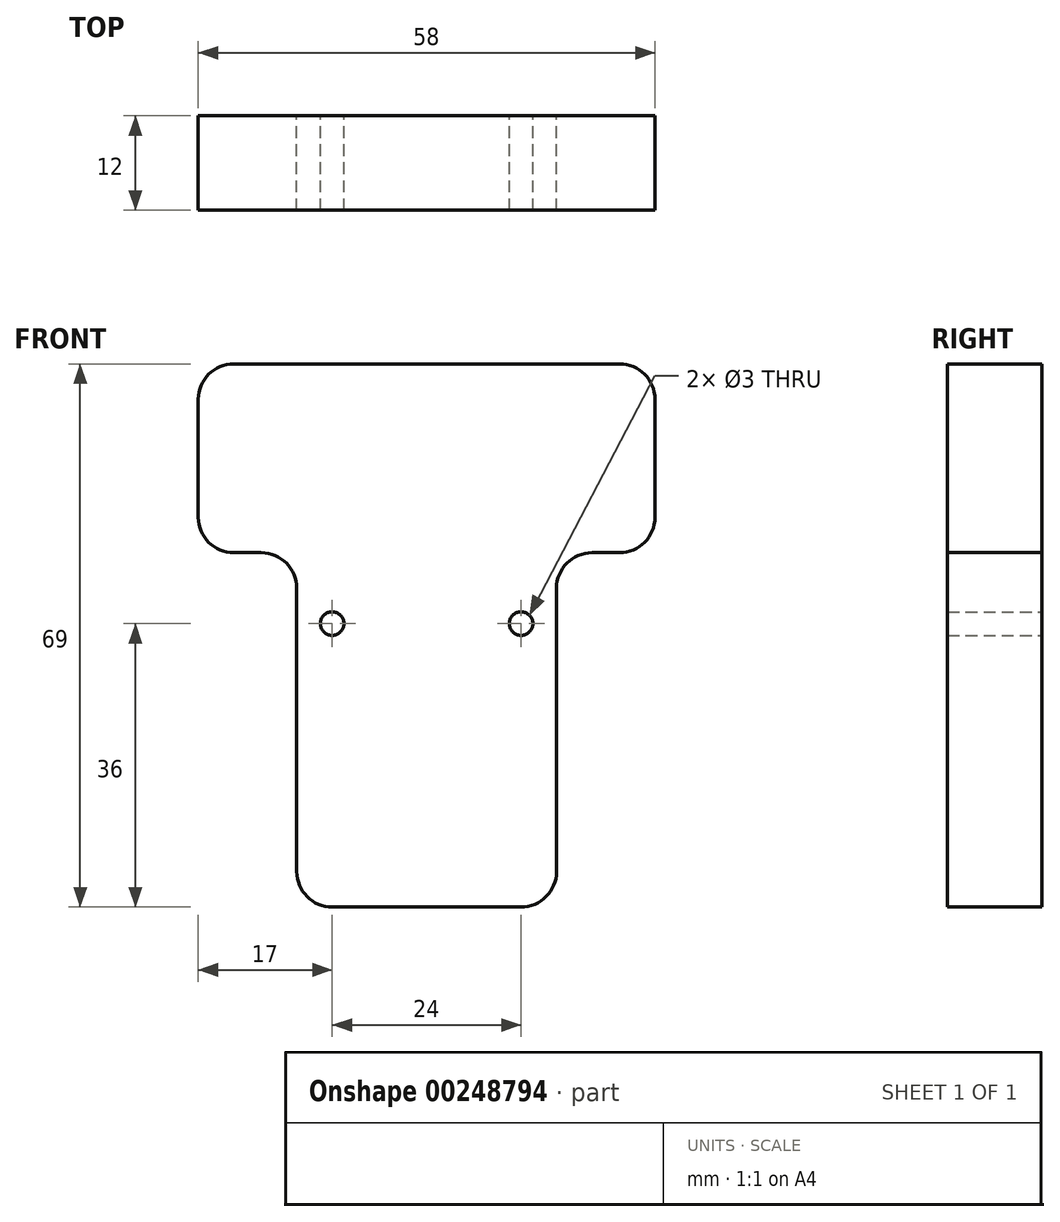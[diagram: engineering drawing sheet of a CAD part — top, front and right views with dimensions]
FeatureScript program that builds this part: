
annotation { "Feature Type Name" : "Feature", "Feature Type Description" : "" }
export const myFeature = defineFeature(function(context is Context, id is Id, definition is map)
    precondition{}
    {
        {
            var Q0;
            Q0=qCreatedBy(makeId("Front.planeOp"),FACE);
            var sketch = newSketch(context, id + "F0", { "sketchPlane" : qUnion([Q0])});
            skLineSegment(sketch, "E0", {"start": v(-16.5, -36) * mm, "end": v(-16.5, 9) * mm});
            skLineSegment(sketch, "E1", {"start": v(-16.5, 9) * mm, "end": v(-29, 9) * mm});
            skLineSegment(sketch, "E2", {"start": v(-29, 9) * mm, "end": v(-29, 33) * mm});
            skLineSegment(sketch, "E3.MirrorCS", {"start": v(16.5, 9) * mm, "end": v(29, 9) * mm});
            skLineSegment(sketch, "E4.MirrorCS", {"start": v(29, 9) * mm, "end": v(29, 33) * mm});
            skLineSegment(sketch, "E5.MirrorCS", {"start": v(16.5, -36) * mm, "end": v(16.5, 9) * mm});
            skLineSegment(sketch, "E6", {"start": v(-29, 33) * mm, "end": v(29, 33) * mm});
            skLineSegment(sketch, "E7", {"start": v(16.5, -36) * mm, "end": v(-16.5, -36) * mm});
            skCircle(sketch, "E8", {"center": v(-12, 0) * mm, "radius": 1.5 * mm});
            skCircle(sketch, "E9.MirrorC", {"center": v(12, 0) * mm, "radius": 1.5 * mm});
            skSolve(sketch);
        }
        {
            var Q0;
            Q0=makeQuery(id+"F0.imprint","IMPRINT",FACE,{"disambiguationData":[TD([[makeQuery(id+"F0.imprint","IMPRINT",EDGE,{"derivedFrom":sQuery(id+"F0.wireOp",EDGE,"E0")}),-1.0]])]});
            extrude(context, id + "F1", {"entities" : qUnion([Q0]), "depth" : 12 * mm, "offsetDistance" : 25 * mm});
        }
        {
            var Q0;
            Q0=makeQuery(id+"F1.opExtrude","SWEPT_EDGE",EDGE,{"disambiguationData":[OSD([sQuery(id+"F0.wireOp",EDGE,"E2"),sQuery(id+"F0.wireOp",EDGE,"E6")])]});
            var Q1;
            Q1=makeQuery(id+"F1.opExtrude","SWEPT_EDGE",EDGE,{"disambiguationData":[OSD([sQuery(id+"F0.wireOp",EDGE,"E1"),sQuery(id+"F0.wireOp",EDGE,"E2")])]});
            var Q2;
            Q2=makeQuery(id+"F1.opExtrude","SWEPT_EDGE",EDGE,{"disambiguationData":[OSD([sQuery(id+"F0.wireOp",EDGE,"E0"),sQuery(id+"F0.wireOp",EDGE,"E1")])]});
            var Q3;
            Q3=makeQuery(id+"F1.opExtrude","SWEPT_EDGE",EDGE,{"disambiguationData":[OSD([sQuery(id+"F0.wireOp",EDGE,"E0"),sQuery(id+"F0.wireOp",EDGE,"E7")])]});
            var Q4;
            Q4=makeQuery(id+"F1.opExtrude","SWEPT_EDGE",EDGE,{"disambiguationData":[OSD([sQuery(id+"F0.wireOp",EDGE,"E5.MirrorCS"),sQuery(id+"F0.wireOp",EDGE,"E7")])]});
            var Q5;
            Q5=makeQuery(id+"F1.opExtrude","SWEPT_EDGE",EDGE,{"disambiguationData":[OSD([sQuery(id+"F0.wireOp",EDGE,"E3.MirrorCS"),sQuery(id+"F0.wireOp",EDGE,"E5.MirrorCS")])]});
            var Q6;
            Q6=makeQuery(id+"F1.opExtrude","SWEPT_EDGE",EDGE,{"disambiguationData":[OSD([sQuery(id+"F0.wireOp",EDGE,"E3.MirrorCS"),sQuery(id+"F0.wireOp",EDGE,"E4.MirrorCS")])]});
            var Q7;
            Q7=makeQuery(id+"F1.opExtrude","SWEPT_EDGE",EDGE,{"disambiguationData":[OSD([sQuery(id+"F0.wireOp",EDGE,"E4.MirrorCS"),sQuery(id+"F0.wireOp",EDGE,"E6")])]});
            fillet(context, id + "F2", {"entities" : qUnion([Q0, Q1, Q2, Q3, Q4, Q5, Q6, Q7]), "radius" : 4.5 * mm, "tangentPropagation" : true, "allowEdgeOverflow" : false});
        }
    });
